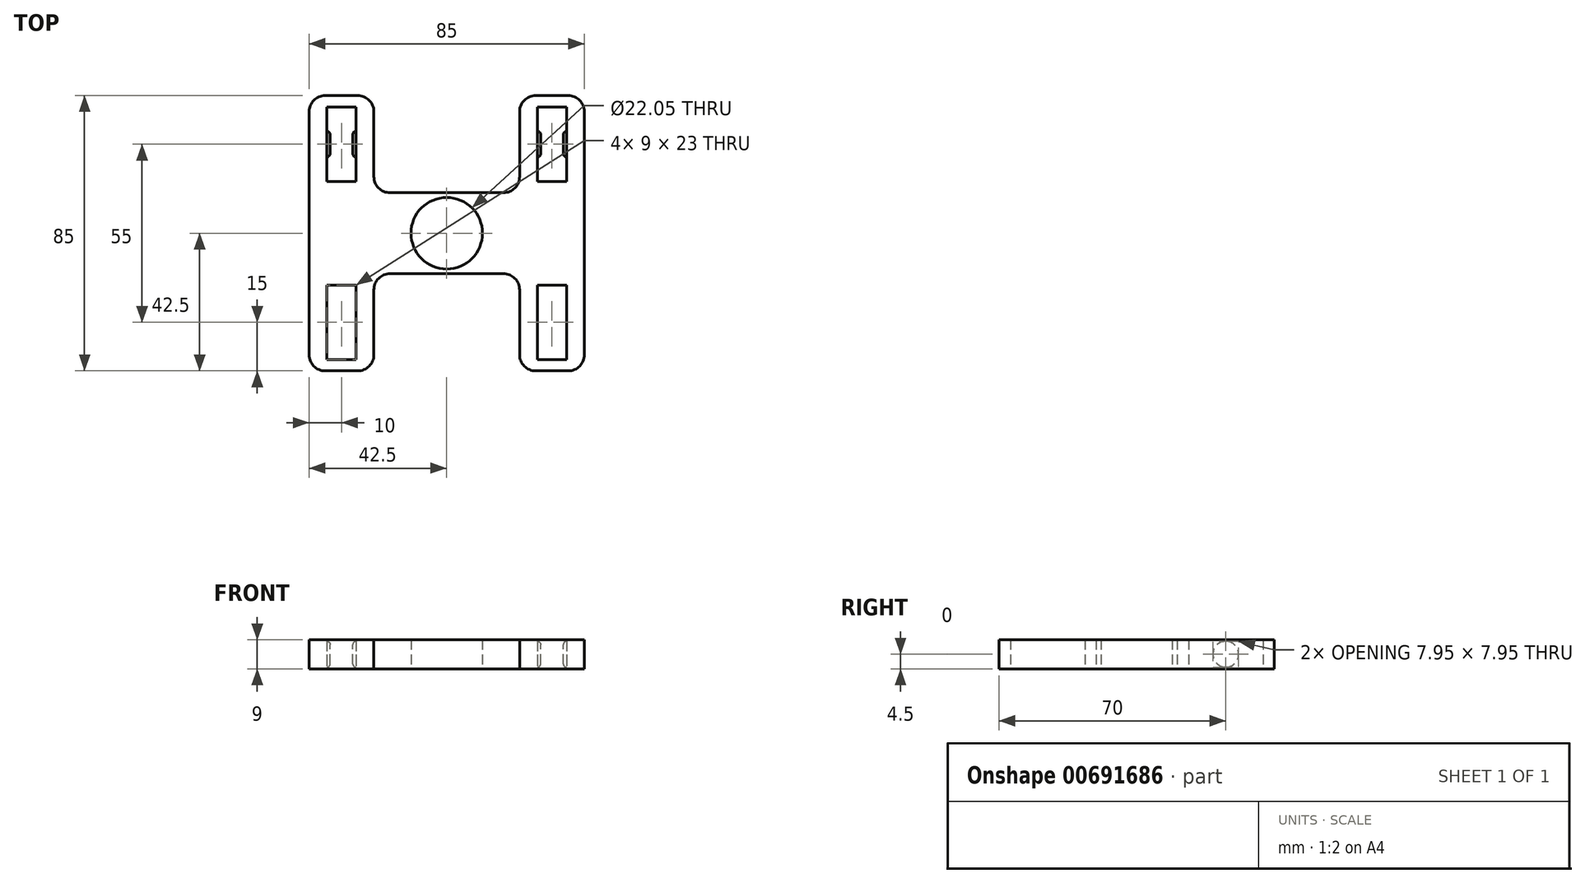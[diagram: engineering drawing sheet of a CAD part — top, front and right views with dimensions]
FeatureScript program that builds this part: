
annotation { "Feature Type Name" : "Feature", "Feature Type Description" : "" }
export const myFeature = defineFeature(function(context is Context, id is Id, definition is map)
    precondition{}
    {
        {
            var Q0;
            Q0=qCreatedBy(makeId("Top.planeOp"),FACE);
            var sketch = newSketch(context, id + "F0", { "sketchPlane" : qUnion([Q0])});
            skCircle(sketch, "E0", {"center": v(0, 0) * mm, "radius": 11.03 * mm});
            skLineSegment(sketch, "E1.bottom", {"start": v(22.5, -12.5) * mm, "end": v(-22.5, -12.5) * mm});
            skLineSegment(sketch, "E1.top", {"start": v(22.5, 12.5) * mm, "end": v(-22.5, 12.5) * mm});
            skLineSegment(sketch, "E1.left", {"start": v(22.5, -12.5) * mm, "end": v(22.5, 12.5) * mm});
            skLineSegment(sketch, "E1.right", {"start": v(-22.5, -12.5) * mm, "end": v(-22.5, 12.5) * mm});
            skLineSegment(sketch, "E2", {"start": v(-22.5, 12.5) * mm, "end": v(-22.5, 42.5) * mm});
            skLineSegment(sketch, "E3", {"start": v(-22.5, 42.5) * mm, "end": v(-42.5, 42.5) * mm});
            skLineSegment(sketch, "E4", {"start": v(-42.5, 42.5) * mm, "end": v(-42.5, -42.5) * mm});
            skLineSegment(sketch, "E5", {"start": v(-42.5, -42.5) * mm, "end": v(-22.5, -42.5) * mm});
            skLineSegment(sketch, "E6", {"start": v(-22.5, -42.5) * mm, "end": v(-22.5, -12.5) * mm});
            skLineSegment(sketch, "E7", {"start": v(22.5, 12.5) * mm, "end": v(22.5, 42.5) * mm});
            skLineSegment(sketch, "E8", {"start": v(22.5, 42.5) * mm, "end": v(42.5, 42.5) * mm});
            skLineSegment(sketch, "E9", {"start": v(42.5, 42.5) * mm, "end": v(42.5, -42.5) * mm});
            skLineSegment(sketch, "E10", {"start": v(42.5, -42.5) * mm, "end": v(22.5, -42.5) * mm});
            skLineSegment(sketch, "E11", {"start": v(22.5, -42.5) * mm, "end": v(22.5, -12.5) * mm});
            skLineSegment(sketch, "E12", {"start": v(-32.5, 42.5) * mm, "end": v(-32.5, 27.5) * mm});
            skPoint(sketch, "E12.endSnap0", {"position": v(-22.5, 27.5) * mm});
            skLineSegment(sketch, "E13.bottom", {"start": v(-28, 16) * mm, "end": v(-37, 16) * mm});
            skLineSegment(sketch, "E13.top", {"start": v(-28, 39) * mm, "end": v(-37, 39) * mm});
            skLineSegment(sketch, "E13.left", {"start": v(-28, 16) * mm, "end": v(-28, 39) * mm});
            skLineSegment(sketch, "E13.right", {"start": v(-37, 16) * mm, "end": v(-37, 39) * mm});
            skPoint(sketch, "E13.middle", {"position": v(-32.5, 27.5) * mm});
            skLineSegment(sketch, "E14", {"start": v(-32.5, -42.5) * mm, "end": v(-32.5, -27.5) * mm});
            skPoint(sketch, "E14.endSnap0", {"position": v(-22.5, -27.5) * mm});
            skLineSegment(sketch, "E15", {"start": v(32.5, -42.5) * mm, "end": v(32.5, -27.5) * mm});
            skPoint(sketch, "E15.endSnap0", {"position": v(22.5, -27.5) * mm});
            skLineSegment(sketch, "E16", {"start": v(32.5, 42.5) * mm, "end": v(32.5, 27.5) * mm});
            skPoint(sketch, "E16.endSnap0", {"position": v(22.5, 27.5) * mm});
            skLineSegment(sketch, "E17.bottom", {"start": v(37, 16) * mm, "end": v(28, 16) * mm});
            skLineSegment(sketch, "E17.top", {"start": v(37, 39) * mm, "end": v(28, 39) * mm});
            skLineSegment(sketch, "E17.left", {"start": v(37, 16) * mm, "end": v(37, 39) * mm});
            skLineSegment(sketch, "E17.right", {"start": v(28, 16) * mm, "end": v(28, 39) * mm});
            skPoint(sketch, "E17.middle", {"position": v(32.5, 27.5) * mm});
            skLineSegment(sketch, "E18.bottom", {"start": v(37, -39) * mm, "end": v(28, -39) * mm});
            skLineSegment(sketch, "E18.top", {"start": v(37, -16) * mm, "end": v(28, -16) * mm});
            skLineSegment(sketch, "E18.left", {"start": v(37, -39) * mm, "end": v(37, -16) * mm});
            skLineSegment(sketch, "E18.right", {"start": v(28, -39) * mm, "end": v(28, -16) * mm});
            skPoint(sketch, "E18.middle", {"position": v(32.5, -27.5) * mm});
            skLineSegment(sketch, "E19.bottom", {"start": v(-28, -39) * mm, "end": v(-37, -39) * mm});
            skLineSegment(sketch, "E19.top", {"start": v(-28, -16) * mm, "end": v(-37, -16) * mm});
            skLineSegment(sketch, "E19.left", {"start": v(-28, -39) * mm, "end": v(-28, -16) * mm});
            skLineSegment(sketch, "E19.right", {"start": v(-37, -39) * mm, "end": v(-37, -16) * mm});
            skPoint(sketch, "E19.middle", {"position": v(-32.5, -27.5) * mm});
            skSolve(sketch);
        }
        {
            var Q0;
            Q0=makeQuery(id+"F0.imprint","IMPRINT",FACE,{"disambiguationData":[TD([[makeQuery(id+"F0.imprint","IMPRINT",EDGE,{"derivedFrom":sQuery(id+"F0.wireOp",EDGE,"E1.right")}),1.0]])]});
            var Q1;
            Q1=makeQuery(id+"F0.imprint","IMPRINT",FACE,{"disambiguationData":[TD([[makeQuery(id+"F0.imprint","IMPRINT",EDGE,{"derivedFrom":sQuery(id+"F0.wireOp",EDGE,"E0")}),-1.0]])]});
            var Q2;
            Q2=makeQuery(id+"F0.imprint","IMPRINT",FACE,{"disambiguationData":[TD([[makeQuery(id+"F0.imprint","IMPRINT",EDGE,{"derivedFrom":sQuery(id+"F0.wireOp",EDGE,"E1.left")}),-1.0]])]});
            extrude(context, id + "F1", {"entities" : qUnion([Q0, Q1, Q2]), "endBound" : BoundingType.SYMMETRIC, "depth" : 9 * mm, "offsetDistance" : 25 * mm});
        }
        {
            var Q0;
            Q0=makeQuery(id+"F1.opExtrude","SWEPT_FACE",FACE,{"disambiguationData":[OSD([sQuery(id+"F0.wireOp",EDGE,"E13.left")])]});
            var sketch = newSketch(context, id + "F2", { "sketchPlane" : qUnion([Q0])});
            skCircle(sketch, "E20", {"center": v(-27.5, 0) * mm, "radius": 3.98 * mm});
            skPoint(sketch, "E20.centerSnap0", {"position": v(-16, 0) * mm});
            skPoint(sketch, "E20.centerSnap1", {"position": v(-27.5, 4.5) * mm});
            skLineSegment(sketch, "E21", {"start": v(-27.5, 0) * mm, "end": v(39, 0) * mm});
            skLineSegment(sketch, "E22", {"start": v(39, 0) * mm, "end": v(16, 0) * mm});
            skCircle(sketch, "E23", {"center": v(27.5, 0) * mm, "radius": 3.98 * mm});
            skSolve(sketch);
        }
        {
            var Q0;
            {var subQ0=sQuery(id+"F2.wireOp",EDGE,"E23");var subQ1=sQuery(id+"F2.wireOp",EDGE,"E22");var subQ2=makeQuery(id+"F2.imprint","INTERSECT",VERTEX,{"disambiguationData":[OD(0.0)],"derivedFrom":[subQ1,subQ0]});Q0=makeQuery(id+"F2.imprint","IMPRINT",FACE,{"disambiguationData":[TD([[makeQuery(id+"F2.imprint","IMPRINT",EDGE,{"disambiguationData":[TD([[subQ2,-1.0]])],"derivedFrom":subQ1}),-1.0]])]});}
            var Q1;
            {var subQ0=sQuery(id+"F2.wireOp",EDGE,"E23");var subQ1=sQuery(id+"F2.wireOp",EDGE,"E22");var subQ2=makeQuery(id+"F2.imprint","INTERSECT",VERTEX,{"disambiguationData":[OD(0.0)],"derivedFrom":[subQ1,subQ0]});Q1=makeQuery(id+"F2.imprint","IMPRINT",FACE,{"disambiguationData":[TD([[makeQuery(id+"F2.imprint","IMPRINT",EDGE,{"disambiguationData":[TD([[subQ2,-1.0]])],"derivedFrom":subQ1}),1.0]])]});}
            var Q2;
            Q2=makeQuery(id+"F2.imprint","IMPRINT",FACE,{"disambiguationData":[TD([[makeQuery(id+"F2.imprint","IMPRINT",EDGE,{"derivedFrom":sQuery(id+"F2.wireOp",EDGE,"E20")}),1.0]])]});
            extrude(context, id + "F3", {"entities" : qUnion([Q0, Q1, Q2]), "operationType" : NewBodyOperationType.ADD, "depth" : 11.8 * mm, "offsetDistance" : 25 * mm, "hasSecondDirection" : true, "secondDirectionOppositeDirection" : true, "secondDirectionDepth" : 66.6 * mm});
        }
        {
            var Q0;
            Q0=qCreatedBy(makeId("Top.planeOp"),FACE);
            var sketch = newSketch(context, id + "F4", { "sketchPlane" : qUnion([Q0])});
            skLineSegment(sketch, "E24", {"start": v(0, 0) * mm, "end": v(-32.5, 0) * mm});
            skLineSegment(sketch, "E25", {"start": v(-32.5, 0) * mm, "end": v(-32.5, 27.5) * mm});
            skLineSegment(sketch, "E26.bottom", {"start": v(-29, 17) * mm, "end": v(-36, 17) * mm});
            skLineSegment(sketch, "E26.top", {"start": v(-29, 38) * mm, "end": v(-36, 38) * mm});
            skLineSegment(sketch, "E26.left", {"start": v(-29, 17) * mm, "end": v(-29, 38) * mm});
            skLineSegment(sketch, "E26.right", {"start": v(-36, 17) * mm, "end": v(-36, 38) * mm});
            skPoint(sketch, "E26.middle", {"position": v(-32.5, 27.5) * mm});
            skLineSegment(sketch, "E27.MirrorCS", {"start": v(-36, -17) * mm, "end": v(-36, -38) * mm});
            skLineSegment(sketch, "E28.MirrorCS", {"start": v(-29, -17) * mm, "end": v(-29, -38) * mm});
            skPoint(sketch, "E29.MirrorP", {"position": v(-32.5, -27.5) * mm});
            skLineSegment(sketch, "E30.MirrorCS", {"start": v(-29, -17) * mm, "end": v(-36, -17) * mm});
            skLineSegment(sketch, "E31.MirrorCS", {"start": v(-29, -38) * mm, "end": v(-36, -38) * mm});
            skLineSegment(sketch, "E32", {"start": v(0, 0) * mm, "end": v(0, 30) * mm});
            skLineSegment(sketch, "E33.MirrorCS", {"start": v(36, -17) * mm, "end": v(36, -38) * mm});
            skLineSegment(sketch, "E34.MirrorCS", {"start": v(29, -17) * mm, "end": v(29, -38) * mm});
            skPoint(sketch, "E35.MirrorP", {"position": v(32.5, -27.5) * mm});
            skLineSegment(sketch, "E36.MirrorCS", {"start": v(29, -17) * mm, "end": v(36, -17) * mm});
            skLineSegment(sketch, "E37.MirrorCS", {"start": v(29, -38) * mm, "end": v(36, -38) * mm});
            skLineSegment(sketch, "E38.MirrorCS", {"start": v(36, 17) * mm, "end": v(36, 38) * mm});
            skLineSegment(sketch, "E39.MirrorCS", {"start": v(29, 17) * mm, "end": v(29, 38) * mm});
            skLineSegment(sketch, "E40.MirrorCS", {"start": v(29, 38) * mm, "end": v(36, 38) * mm});
            skLineSegment(sketch, "E41.MirrorCS", {"start": v(29, 17) * mm, "end": v(36, 17) * mm});
            skPoint(sketch, "E42.MirrorP", {"position": v(32.5, 27.5) * mm});
            skLineSegment(sketch, "E43.bottom", {"start": v(22.5, 16.58) * mm, "end": v(-22.5, 16.58) * mm});
            skLineSegment(sketch, "E43.top", {"start": v(22.5, 43.42) * mm, "end": v(-22.5, 43.42) * mm});
            skLineSegment(sketch, "E43.left", {"start": v(22.5, 16.58) * mm, "end": v(22.5, 43.42) * mm});
            skLineSegment(sketch, "E43.right", {"start": v(-22.5, 16.58) * mm, "end": v(-22.5, 43.42) * mm});
            skPoint(sketch, "E43.middle", {"position": v(0, 30) * mm});
            skLineSegment(sketch, "E44.MirrorCS", {"start": v(22.5, -16.58) * mm, "end": v(-22.5, -16.58) * mm});
            skLineSegment(sketch, "E45.MirrorCS", {"start": v(-22.5, -16.58) * mm, "end": v(-22.5, -43.42) * mm});
            skLineSegment(sketch, "E46.MirrorCS", {"start": v(22.5, -43.42) * mm, "end": v(-22.5, -43.42) * mm});
            skLineSegment(sketch, "E47.MirrorCS", {"start": v(22.5, -16.58) * mm, "end": v(22.5, -43.42) * mm});
            skSolve(sketch);
        }
        {
            var Q0;
            Q0=makeQuery(id+"F4.imprint","IMPRINT",FACE,{"disambiguationData":[TD([[makeQuery(id+"F4.imprint","IMPRINT",EDGE,{"derivedFrom":sQuery(id+"F4.wireOp",EDGE,"E26.top")}),1.0]])]});
            var Q1;
            Q1=makeQuery(id+"F4.imprint","IMPRINT",FACE,{"disambiguationData":[TD([[makeQuery(id+"F4.imprint","IMPRINT",EDGE,{"derivedFrom":sQuery(id+"F4.wireOp",EDGE,"E27.MirrorCS")}),1.0]])]});
            var Q2;
            Q2=makeQuery(id+"F4.imprint","IMPRINT",FACE,{"disambiguationData":[TD([[makeQuery(id+"F4.imprint","IMPRINT",EDGE,{"derivedFrom":sQuery(id+"F4.wireOp",EDGE,"E44.MirrorCS")}),1.0]])]});
            var Q3;
            Q3=makeQuery(id+"F4.imprint","IMPRINT",FACE,{"disambiguationData":[TD([[makeQuery(id+"F4.imprint","IMPRINT",EDGE,{"derivedFrom":sQuery(id+"F4.wireOp",EDGE,"E43.top")}),1.0]])]});
            var Q4;
            Q4=makeQuery(id+"F4.imprint","IMPRINT",FACE,{"disambiguationData":[TD([[makeQuery(id+"F4.imprint","IMPRINT",EDGE,{"derivedFrom":sQuery(id+"F4.wireOp",EDGE,"E38.MirrorCS")}),1.0]])]});
            var Q5;
            Q5=makeQuery(id+"F4.imprint","IMPRINT",FACE,{"disambiguationData":[TD([[makeQuery(id+"F4.imprint","IMPRINT",EDGE,{"derivedFrom":sQuery(id+"F4.wireOp",EDGE,"E33.MirrorCS")}),-1.0]])]});
            extrude(context, id + "F5", {"entities" : qUnion([Q0, Q1, Q2, Q3, Q4, Q5]), "operationType" : NewBodyOperationType.REMOVE, "endBound" : BoundingType.SYMMETRIC, "oppositeDirection" : true, "depth" : 25 * mm, "offsetDistance" : 25 * mm});
        }
        {
            var Q0;
            Q0=makeQuery(id+"F1.opExtrude","SWEPT_EDGE",EDGE,{"disambiguationData":[OSD([sQuery(id+"F0.wireOp",EDGE,"E1.bottom"),sQuery(id+"F0.wireOp",EDGE,"E1.right"),sQuery(id+"F0.wireOp",EDGE,"E6")])]});
            var Q1;
            Q1=makeQuery(id+"F1.opExtrude","SWEPT_EDGE",EDGE,{"disambiguationData":[OSD([sQuery(id+"F0.wireOp",EDGE,"E1.bottom"),sQuery(id+"F0.wireOp",EDGE,"E1.left"),sQuery(id+"F0.wireOp",EDGE,"E11")])]});
            var Q2;
            Q2=makeQuery(id+"F1.opExtrude","SWEPT_EDGE",EDGE,{"disambiguationData":[OSD([sQuery(id+"F0.wireOp",EDGE,"E10"),sQuery(id+"F0.wireOp",EDGE,"E11")])]});
            var Q3;
            Q3=makeQuery(id+"F1.opExtrude","SWEPT_EDGE",EDGE,{"disambiguationData":[OSD([sQuery(id+"F0.wireOp",EDGE,"E5"),sQuery(id+"F0.wireOp",EDGE,"E6")])]});
            var Q4;
            Q4=makeQuery(id+"F1.opExtrude","SWEPT_EDGE",EDGE,{"disambiguationData":[OSD([sQuery(id+"F0.wireOp",EDGE,"E4"),sQuery(id+"F0.wireOp",EDGE,"E5")])]});
            var Q5;
            Q5=makeQuery(id+"F1.opExtrude","SWEPT_EDGE",EDGE,{"disambiguationData":[OSD([sQuery(id+"F0.wireOp",EDGE,"E9"),sQuery(id+"F0.wireOp",EDGE,"E10")])]});
            var Q6;
            Q6=makeQuery(id+"F1.opExtrude","SWEPT_EDGE",EDGE,{"disambiguationData":[OSD([sQuery(id+"F0.wireOp",EDGE,"E8"),sQuery(id+"F0.wireOp",EDGE,"E9")])]});
            var Q7;
            Q7=makeQuery(id+"F1.opExtrude","SWEPT_EDGE",EDGE,{"disambiguationData":[OSD([sQuery(id+"F0.wireOp",EDGE,"E7"),sQuery(id+"F0.wireOp",EDGE,"E8")])]});
            var Q8;
            Q8=makeQuery(id+"F1.opExtrude","SWEPT_EDGE",EDGE,{"disambiguationData":[OSD([sQuery(id+"F0.wireOp",EDGE,"E2"),sQuery(id+"F0.wireOp",EDGE,"E3")])]});
            var Q9;
            Q9=makeQuery(id+"F1.opExtrude","SWEPT_EDGE",EDGE,{"disambiguationData":[OSD([sQuery(id+"F0.wireOp",EDGE,"E1.top"),sQuery(id+"F0.wireOp",EDGE,"E1.right"),sQuery(id+"F0.wireOp",EDGE,"E2")])]});
            var Q10;
            Q10=makeQuery(id+"F1.opExtrude","SWEPT_EDGE",EDGE,{"disambiguationData":[OSD([sQuery(id+"F0.wireOp",EDGE,"E1.top"),sQuery(id+"F0.wireOp",EDGE,"E1.left"),sQuery(id+"F0.wireOp",EDGE,"E7")])]});
            var Q11;
            Q11=makeQuery(id+"F1.opExtrude","SWEPT_EDGE",EDGE,{"disambiguationData":[OSD([sQuery(id+"F0.wireOp",EDGE,"E3"),sQuery(id+"F0.wireOp",EDGE,"E4")])]});
            fillet(context, id + "F6", {"entities" : qUnion([Q0, Q1, Q2, Q3, Q4, Q5, Q6, Q7, Q8, Q9, Q10, Q11]), "radius" : 5 * mm, "tangentPropagation" : true, "allowEdgeOverflow" : false});
        }
        {
            var Q0;
            Q0=makeQuery(id+"F5.boolean.opBoolean","COPY",FACE,{"derivedFrom":makeQuery(id+"F5.opExtrude","SWEPT_FACE",FACE,{"disambiguationData":[OSD([sQuery(id+"F4.wireOp",EDGE,"E27.MirrorCS")])]})});
            var Q1;
            Q1=makeQuery(id+"F5.boolean.opBoolean","COPY",FACE,{"derivedFrom":makeQuery(id+"F5.opExtrude","SWEPT_FACE",FACE,{"disambiguationData":[OSD([sQuery(id+"F4.wireOp",EDGE,"E28.MirrorCS")])]})});
            var Q2;
            Q2=makeQuery(id+"F5.boolean.opBoolean","COPY",FACE,{"derivedFrom":makeQuery(id+"F5.opExtrude","SWEPT_FACE",FACE,{"disambiguationData":[OSD([sQuery(id+"F4.wireOp",EDGE,"E34.MirrorCS")])]})});
            var Q3;
            Q3=makeQuery(id+"F5.boolean.opBoolean","COPY",FACE,{"derivedFrom":makeQuery(id+"F5.opExtrude","SWEPT_FACE",FACE,{"disambiguationData":[OSD([sQuery(id+"F4.wireOp",EDGE,"E33.MirrorCS")])]})});
            var Q4;
            Q4=makeQuery(id+"F5.boolean.opBoolean","COPY",FACE,{"derivedFrom":makeQuery(id+"F5.opExtrude","SWEPT_FACE",FACE,{"disambiguationData":[OSD([sQuery(id+"F4.wireOp",EDGE,"E38.MirrorCS")])]})});
            var Q5;
            Q5=makeQuery(id+"F5.boolean.opBoolean","COPY",FACE,{"derivedFrom":makeQuery(id+"F5.opExtrude","SWEPT_FACE",FACE,{"disambiguationData":[OSD([sQuery(id+"F4.wireOp",EDGE,"E39.MirrorCS")])]})});
            var Q6;
            Q6=makeQuery(id+"F5.boolean.opBoolean","COPY",FACE,{"derivedFrom":makeQuery(id+"F5.opExtrude","SWEPT_FACE",FACE,{"disambiguationData":[OSD([sQuery(id+"F4.wireOp",EDGE,"E26.right")])]})});
            var Q7;
            Q7=makeQuery(id+"F5.boolean.opBoolean","COPY",FACE,{"derivedFrom":makeQuery(id+"F5.opExtrude","SWEPT_FACE",FACE,{"disambiguationData":[OSD([sQuery(id+"F4.wireOp",EDGE,"E26.left")])]})});
            fillet(context, id + "F7", {"entities" : qUnion([Q0, Q1, Q2, Q3, Q4, Q5, Q6, Q7]), "radius" : 1 * mm, "tangentPropagation" : true, "allowEdgeOverflow" : false});
        }
    });
